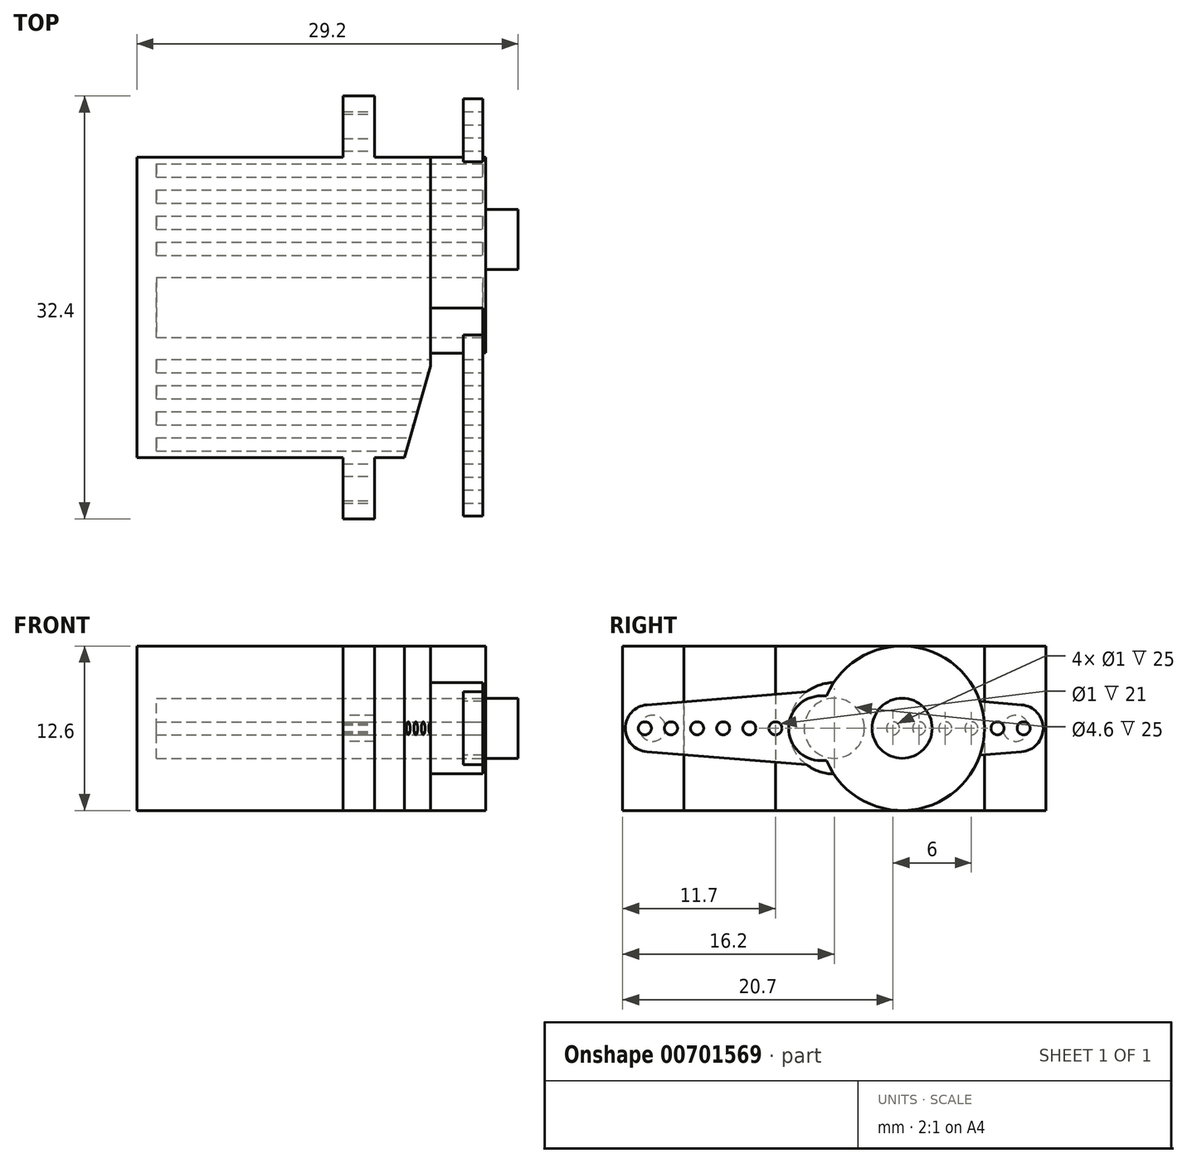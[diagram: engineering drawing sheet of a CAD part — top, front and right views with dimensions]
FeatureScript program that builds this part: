
annotation { "Feature Type Name" : "Feature", "Feature Type Description" : "" }
export const myFeature = defineFeature(function(context is Context, id is Id, definition is map)
    precondition{}
    {
        {
            var Q0;
            Q0=qCreatedBy(makeId("Top.planeOp"),FACE);
            var sketch = newSketch(context, id + "F0", { "sketchPlane" : qUnion([Q0])});
            skLineSegment(sketch, "E0.bottom", {"start": v(-22.5, 11.5) * mm, "end": v(0, 11.5) * mm});
            skLineSegment(sketch, "E0.top", {"start": v(-22.5, -11.5) * mm, "end": v(0, -11.5) * mm});
            skLineSegment(sketch, "E0.left", {"start": v(-22.5, 11.5) * mm, "end": v(-22.5, -11.5) * mm});
            skLineSegment(sketch, "E0.right", {"start": v(0, 11.5) * mm, "end": v(0, -11.5) * mm});
            skPoint(sketch, "E1", {"position": v(-22.5, 0) * mm});
            skSolve(sketch);
        }
        {
            var Q0;
            Q0=qSketchRegion(id+"F0",true);
            extrude(context, id + "F1", {"entities" : qUnion([Q0]), "endBound" : BoundingType.SYMMETRIC, "depth" : 12.6 * mm, "offsetDistance" : 25 * mm});
        }
        {
            var Q0;
            Q0=makeQuery(id+"F1.opExtrude","SWEPT_EDGE",EDGE,{"disambiguationData":[OSD([sQuery(id+"F0.wireOp",EDGE,"E0.top"),sQuery(id+"F0.wireOp",EDGE,"E0.right")])]});
            chamfer(context, id + "F2", {"entities" : qUnion([Q0]), "chamferType" : ChamferType.TWO_OFFSETS, "width1" : 7 * mm, "oppositeDirection" : false, "width2" : 2 * mm, "tangentPropagation" : true});
        }
        {
            var Q0;
            Q0=makeQuery(id+"F1.opExtrude","SWEPT_FACE",FACE,{"disambiguationData":[OSD([sQuery(id+"F0.wireOp",EDGE,"E0.right")])]});
            cPlane(context, id + "F3", {"entities" : qUnion([Q0]), "cplaneType" : CPlaneType.OFFSET, "offset" : (22.5 - 15.8) * mm, "oppositeDirection" : true, "width" : 150 * mm, "height" : 150 * mm});
        }
        {
            var Q0;
            Q0=qCreatedBy(id+"F3.planeOp",FACE);
            var sketch = newSketch(context, id + "F4", { "sketchPlane" : qUnion([Q0])});
            skLineSegment(sketch, "E2.bottom", {"start": v(16.2, 6.3) * mm, "end": v(-16.2, 6.3) * mm});
            skLineSegment(sketch, "E2.top", {"start": v(16.2, -6.3) * mm, "end": v(-16.2, -6.3) * mm});
            skLineSegment(sketch, "E2.left", {"start": v(16.2, 6.3) * mm, "end": v(16.2, -6.3) * mm});
            skLineSegment(sketch, "E2.right", {"start": v(-16.2, 6.3) * mm, "end": v(-16.2, -6.3) * mm});
            skPoint(sketch, "E2.middle", {"position": v(0, 0) * mm});
            skCircle(sketch, "E3", {"center": v(-13.9, 0) * mm, "radius": 1 * mm});
            skCircle(sketch, "E4", {"center": v(13.9, 0) * mm, "radius": 1 * mm});
            skLineSegment(sketch, "E5", {"start": v(-13.9, 0) * mm, "end": v(13.9, 0) * mm, "construction": true});
            skSolve(sketch);
        }
        {
            var Q0;
            Q0=qSketchRegion(id+"F4",true);
            extrude(context, id + "F5", {"entities" : qUnion([Q0]), "operationType" : NewBodyOperationType.ADD, "depth" : 2.4 * mm, "offsetDistance" : 25 * mm});
        }
        {
            var Q0;
            Q0=makeQuery(id+"F1.opExtrude","SWEPT_FACE",FACE,{"disambiguationData":[OSD([sQuery(id+"F0.wireOp",EDGE,"E0.right")])]});
            var sketch = newSketch(context, id + "F6", { "sketchPlane" : qUnion([Q0])});
            skCircle(sketch, "E6", {"center": v(5.2, 0) * mm, "radius": 6.3 * mm});
            skArc(sketch, "E7", {"start": v(-1, 2.48) * mm, "mid": v(-3.49, 0) * mm, "end": v(-1, -2.48) * mm});
            skLineSegment(sketch, "E8", {"start": v(-1, -0.36) * mm, "end": v(-1, 0) * mm, "construction": true});
            skLineSegment(sketch, "E9", {"start": v(-1, -2.48) * mm, "end": v(-0.59, -2.48) * mm});
            skLineSegment(sketch, "E10", {"start": v(-1, 2.48) * mm, "end": v(-0.59, 2.48) * mm});
            skSolve(sketch);
        }
        {
            var Q0;
            Q0=qSketchRegion(id+"F6",true);
            extrude(context, id + "F7", {"entities" : qUnion([Q0]), "operationType" : NewBodyOperationType.ADD, "depth" : 4.2 * mm, "offsetDistance" : 25 * mm});
        }
        {
            var Q0;
            Q0=makeQuery(id+"F7.opExtrude","CAP_FACE",FACE,{"disambiguationData":[OSD([sQuery(id+"F6.wireOp",EDGE,"E6"),sQuery(id+"F6.wireOp",EDGE,"E7"),sQuery(id+"F6.wireOp",EDGE,"E9"),sQuery(id+"F6.wireOp",EDGE,"E10")])],"isStart":false});
            var sketch = newSketch(context, id + "F8", { "sketchPlane" : qUnion([Q0])});
            skCircle(sketch, "E11", {"center": v(5.2, 0) * mm, "radius": 2.3 * mm});
            skSolve(sketch);
        }
        {
            var Q0;
            Q0=qSketchRegion(id+"F8",true);
            extrude(context, id + "F9", {"entities" : qUnion([Q0]), "operationType" : NewBodyOperationType.ADD, "depth" : (29.2 - 26.7) * mm, "offsetDistance" : 25 * mm});
        }
        {
            var Q0;
            Q0=qCreatedBy(makeId("Right.planeOp"),FACE);
            var sketch = newSketch(context, id + "F10", { "sketchPlane" : qUnion([Q0])});
            skCircle(sketch, "E12", {"center": v(0, 0) * mm, "radius": 3.5 * mm});
            skSolve(sketch);
        }
        {
            var Q0;
            Q0=qSketchRegion(id+"F10",true);
            extrude(context, id + "F11", {"entities" : qUnion([Q0]), "depth" : 4 * mm, "offsetDistance" : 25 * mm});
        }
        {
            var Q0;
            Q0=makeQuery(id+"F11.opExtrude","CAP_FACE",FACE,{"disambiguationData":[OSD([sQuery(id+"F10.wireOp",EDGE,"E12")])],"isStart":false});
            var sketch = newSketch(context, id + "F12", { "sketchPlane" : qUnion([Q0])});
            skCircle(sketch, "E13", {"center": v(0, 0) * mm, "radius": 2.3 * mm});
            skSolve(sketch);
        }
        {
            var Q0;
            Q0=makeQuery(id+"F11.opExtrude","CAP_FACE",FACE,{"disambiguationData":[OSD([sQuery(id+"F10.wireOp",EDGE,"E12")])],"isStart":false});
            var sketch = newSketch(context, id + "F13", { "sketchPlane" : qUnion([Q0])});
            skLineSegment(sketch, "E14", {"start": v(2.1, 2.8) * mm, "end": v(14.35, 1.8) * mm});
            skLineSegment(sketch, "E15", {"start": v(14.35, -1.8) * mm, "end": v(2.1, -2.8) * mm});
            skPoint(sketch, "E16.visualSharp", {"position": v(36.19, 0) * mm});
            skArc(sketch, "E16.filletArc", {"start": v(14.35, -1.8) * mm, "mid": v(16, 0) * mm, "end": v(14.35, 1.8) * mm});
            skPoint(sketch, "E17", {"position": v(16, 0) * mm});
            skLineSegment(sketch, "E18", {"start": v(0, 6.54) * mm, "end": v(0, 4.42) * mm, "construction": true});
            skLineSegment(sketch, "E19.MirrorCS", {"start": v(-2.1, 2.8) * mm, "end": v(-14.35, 1.8) * mm});
            skLineSegment(sketch, "E20.MirrorCS", {"start": v(-14.35, -1.8) * mm, "end": v(-2.1, -2.8) * mm});
            skArc(sketch, "E21.MirrorCS", {"start": v(-14.35, -1.8) * mm, "mid": v(-16, 0) * mm, "end": v(-14.35, 1.8) * mm});
            skPoint(sketch, "E22.MirrorP", {"position": v(-16, 0) * mm});
            skLineSegment(sketch, "E23", {"start": v(-2.1, 2.8) * mm, "end": v(2.1, 2.8) * mm});
            skLineSegment(sketch, "E24", {"start": v(2.1, -2.8) * mm, "end": v(-2.1, -2.8) * mm});
            skSolve(sketch);
        }
        {
            var Q0;
            Q0=qSketchRegion(id+"F13",true);
            extrude(context, id + "F14", {"entities" : qUnion([Q0]), "operationType" : NewBodyOperationType.ADD, "oppositeDirection" : true, "depth" : 1.5 * mm, "offsetDistance" : 25 * mm});
        }
        {
            var Q0;
            Q0=qSketchRegion(id+"F12",true);
            extrude(context, id + "F15", {"entities" : qUnion([Q0]), "operationType" : NewBodyOperationType.REMOVE, "oppositeDirection" : true, "depth" : 25 * mm, "offsetDistance" : 25 * mm});
        }
        {
            var Q0;
            Q0=makeQuery(id+"F14.boolean.opBoolean","MERGE",FACE,{"derivedFrom":[makeQuery(id+"F11.opExtrude","CAP_FACE",FACE,{"disambiguationData":[OSD([sQuery(id+"F10.wireOp",EDGE,"E12")])],"isStart":false}),makeQuery(id+"F14.opExtrude","CAP_FACE",FACE,{"disambiguationData":[OSD([sQuery(id+"F13.wireOp",EDGE,"E14"),sQuery(id+"F13.wireOp",EDGE,"E15"),sQuery(id+"F13.wireOp",EDGE,"E16.filletArc"),sQuery(id+"F13.wireOp",EDGE,"E19.MirrorCS"),sQuery(id+"F13.wireOp",EDGE,"E20.MirrorCS"),sQuery(id+"F13.wireOp",EDGE,"E21.MirrorCS"),sQuery(id+"F13.wireOp",EDGE,"E23"),sQuery(id+"F13.wireOp",EDGE,"E24")])],"isStart":true})]});
            var sketch = newSketch(context, id + "F16", { "sketchPlane" : qUnion([Q0])});
            skCircle(sketch, "E25", {"center": v(4.5, 0) * mm, "radius": 0.5 * mm});
            skCircle(sketch, "E26.1.0.0", {"center": v(6.5, 0) * mm, "radius": 0.5 * mm});
            skCircle(sketch, "E26.2.0.0", {"center": v(8.5, 0) * mm, "radius": 0.5 * mm});
            skCircle(sketch, "E26.3.0.0", {"center": v(10.5, 0) * mm, "radius": 0.5 * mm});
            skCircle(sketch, "E26.4.0.0", {"center": v(12.5, 0) * mm, "radius": 0.5 * mm});
            skCircle(sketch, "E26.5.0.0", {"center": v(14.5, 0) * mm, "radius": 0.5 * mm});
            skLineSegment(sketch, "E26.direction1", {"start": v(4.5, 0) * mm, "end": v(6.5, 0) * mm, "construction": true});
            skLineSegment(sketch, "E27", {"start": v(0, 7.5) * mm, "end": v(0, 4.47) * mm, "construction": true});
            skCircle(sketch, "E28.MirrorC", {"center": v(-14.5, 0) * mm, "radius": 0.5 * mm});
            skCircle(sketch, "E29.MirrorC", {"center": v(-12.5, 0) * mm, "radius": 0.5 * mm});
            skCircle(sketch, "E30.MirrorC", {"center": v(-10.5, 0) * mm, "radius": 0.5 * mm});
            skCircle(sketch, "E31.MirrorC", {"center": v(-8.5, 0) * mm, "radius": 0.5 * mm});
            skCircle(sketch, "E32.MirrorC", {"center": v(-6.5, 0) * mm, "radius": 0.5 * mm});
            skCircle(sketch, "E33.MirrorC", {"center": v(-4.5, 0) * mm, "radius": 0.5 * mm});
            skSolve(sketch);
        }
        {
            var Q0;
            Q0 = qSketchRegion(id + "F16", true);
            extrude(context, id + "F17", {"entities" : qUnion([Q0]), "operationType" : NewBodyOperationType.REMOVE, "oppositeDirection" : true, "depth" : 25 * mm, "offsetDistance" : 25 * mm});
        }
    });
